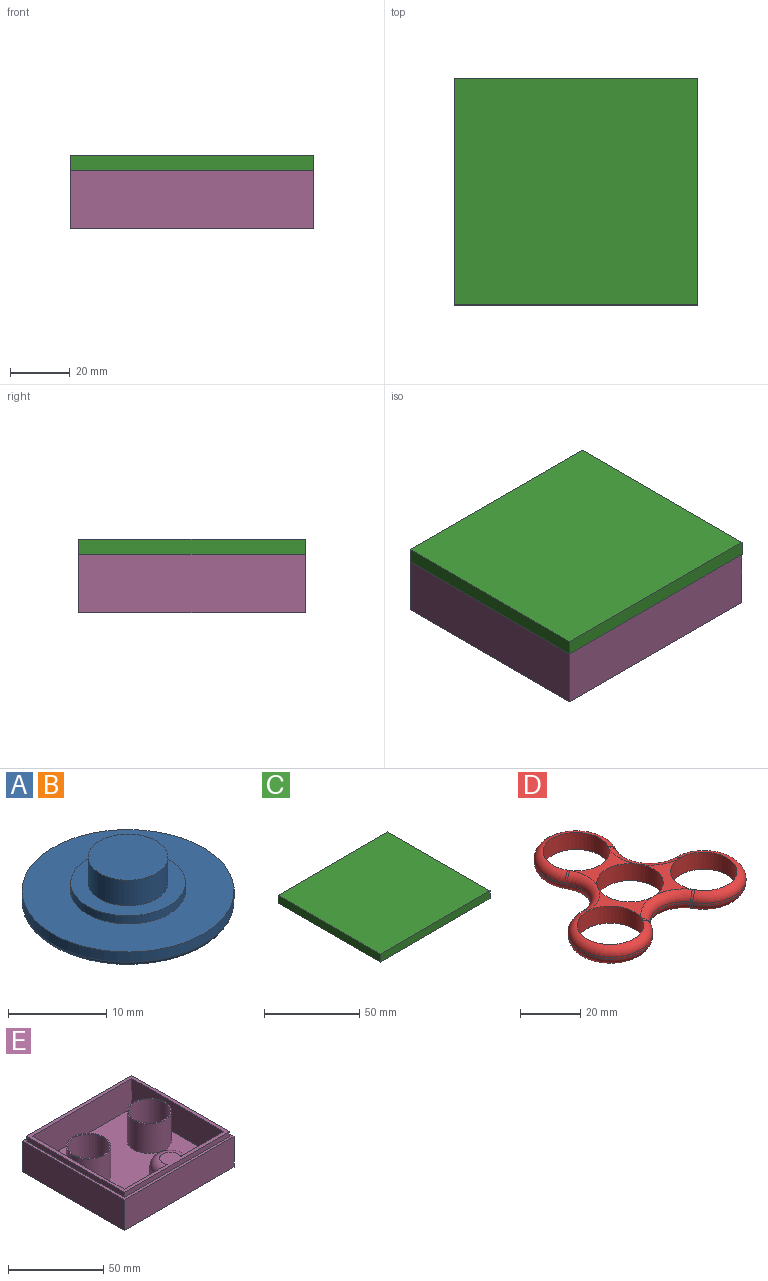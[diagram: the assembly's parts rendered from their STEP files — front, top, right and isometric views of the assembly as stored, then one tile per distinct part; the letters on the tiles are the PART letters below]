
ASSEMBLY  parts=5 mates=4
PART A: 15 faces, bbox 23.4x23.4x6 mm
  f0: plane 20.57x20.57mm, normal (0,0,-1), area 306.2mm2, adj f5,f6,f7,f8,f9,f10,f11
  f1: cylinder r=10.79mm len=21.59mm, axis (0,0,-1), area 86.1mm2, adj f2,f5
  f2: plane 21.59x21.59mm, normal (0,0,1), area 258.9mm2, adj f1,f3
  f3: cylinder r=5.84mm len=11.68mm, axis (0,0,-1), area 37.3mm2, adj f2,f4
  f4: plane 11.68x11.68mm, normal (0,0,1), area 55.2mm2, adj f3,f13
  f5: torus R=10.29mm, axis (0,0,1), area 53.2mm2, adj f0,f1
  f6: plane 9.77x8.45mm, normal (0.65,0.76,0), area 6.6mm2, adj f0,f7,f11,f12
  f7: plane 6.1x0.51mm, normal (0,-1,0), area 3.1mm2, adj f0,f6,f8,f12
  f8: plane 6.49x6.15mm, normal (0.69,0.73,0), area 4.5mm2, adj f0,f7,f9,f12
  f9: plane 10.56x7.83mm, normal (-0.6,-0.8,0), area 6.7mm2, adj f0,f8,f10,f12
  f10: plane 6.1x0.51mm, normal (0,1,0), area 3.1mm2, adj f0,f9,f11,f12
  f11: plane 6.77x5.71mm, normal (-0.76,-0.64,0), area 4.5mm2, adj f0,f6,f10,f12
  f12: plane 14.6x10.56mm, normal (0,0,-1), area 26.2mm2, adj f6,f7,f8,f9,f10,f11
  f13: cylinder r=4.07mm len=8.14mm, axis (0,0,-1), area 81.2mm2, adj f4,f14
  f14: plane 8.14x8.14mm, normal (0,0,1), area 52mm2, adj f13
PART B: same geometry as A
PART C: 6 faces, bbox 81.8x75.9x5.1 mm
  f0: plane 81.79x5.08mm, normal (0,1,0), area 415.5mm2, adj f1,f3,f4,f5
  f1: plane 75.93x5.08mm, normal (-1,0,0), area 385.7mm2, adj f0,f2,f4,f5
  f2: plane 81.79x5.08mm, normal (0,-1,0), area 415.5mm2, adj f1,f3,f4,f5
  f3: plane 75.93x5.08mm, normal (1,0,0), area 385.7mm2, adj f0,f2,f4,f5
  f4: plane 81.79x75.93mm, normal (0,0,1), area 6210.4mm2, adj f0,f1,f2,f3
  f5: plane 81.79x75.93mm, normal (0,0,-1), area 6210.4mm2, adj f0,f1,f2,f3
PART D: 40 faces, bbox 73.9x68.1x7.4 mm
  f0: plane 18.08x12.74mm, normal (0,0,1), area 84.2mm2, adj f9,f12,f30,f38
  f1: plane 22.02x20.07mm, normal (0,0,1), area 84.2mm2, adj f9,f11,f33,f38
  f2: plane 22.02x20.07mm, normal (0,0,-1), area 84.2mm2, adj f9,f10,f23,f24
  f3: plane 22.02x20.07mm, normal (0,0,-1), area 84.2mm2, adj f9,f11,f16,f24
  f4: cylinder r=11.25mm len=16.88mm, axis (0,0,-1), area 19.8mm2, adj f5,f13,f16,f17,f18,f36,f38,f39
  f5: cylinder r=13.97mm len=27.94mm, axis (0,0,-1), area 49.1mm2, adj f4,f6,f20,f37
  f6: cylinder r=11.25mm len=19.49mm, axis (0,0,-1), area 19.8mm2, adj f5,f7,f22,f24,f26,f31,f33,f35
  f7: cylinder r=13.97mm len=27.94mm, axis (0,0,-1), area 49.1mm2, adj f6,f8,f27,f29
  f8: cylinder r=11.26mm len=16.88mm, axis (0,0,-1), area 19.8mm2, adj f7,f13,f21,f23,f25,f28,f30,f32
  f9: cylinder r=10.99mm len=21.97mm, axis (0,0,-1), area 478.6mm2, adj f0,f1,f2,f3,f14,f15,f16,f23
  f10: cylinder r=10.99mm len=21.97mm, axis (0,0,-1), area 478.6mm2, adj f2,f14,f25,f26,f27,f28,f29,f31
  f11: cylinder r=10.99mm len=21.97mm, axis (0,0,-1), area 478.6mm2, adj f1,f3,f18,f20,f22,f35,f37,f39
  f12: cylinder r=10.99mm len=21.97mm, axis (0,0,-1), area 478.6mm2, adj f0,f15,f17,f19,f21,f32,f34,f36
  f13: cylinder r=13.97mm len=27.94mm, axis (0,0,-1), area 49.1mm2, adj f4,f8,f19,f34
  f14: plane 22.02x20.07mm, normal (0,0,1), area 84.2mm2, adj f9,f10,f30,f33
  f15: plane 18.08x12.74mm, normal (0,0,-1), area 84.2mm2, adj f9,f12,f16,f23
  f16: torus R=14.3mm, axis (0,0,1), area 116.6mm2, adj f3,f4,f9,f15,f17,f18
  f17: bspline ~3.88x3.51mm, area 3.6mm2, adj f4,f12,f16,f19
  f18: bspline ~3.16x3.15mm, area 3.6mm2, adj f4,f11,f16,f20
  f19: torus R=10.92mm, axis (0,0,-1), area 255mm2, adj f12,f13,f17,f21
  f20: torus R=10.92mm, axis (0,0,-1), area 255.1mm2, adj f5,f11,f18,f22
  f21: bspline ~3.88x3.51mm, area 3.6mm2, adj f8,f12,f19,f23
  f22: bspline ~3.55x3.38mm, area 3.6mm2, adj f6,f11,f20,f24
  f23: torus R=14.3mm, axis (0,0,1), area 116.6mm2, adj f2,f8,f9,f15,f21,f25
  f24: torus R=14.3mm, axis (0,0,1), area 116.6mm2, adj f2,f3,f6,f9,f22,f26
  f25: bspline ~3.16x3.15mm, area 3.6mm2, adj f8,f10,f23,f27
  f26: bspline ~3.55x3.38mm, area 3.6mm2, adj f6,f10,f24,f27
  f27: torus R=10.92mm, axis (0,0,-1), area 255mm2, adj f7,f10,f25,f26
  f28: bspline ~3.16x3.15mm, area 3.6mm2, adj f8,f10,f29,f30
  f29: torus R=10.92mm, axis (0,0,1), area 255mm2, adj f7,f10,f28,f31
  f30: torus R=14.3mm, axis (0,0,1), area 116.6mm2, adj f0,f8,f9,f14,f28,f32
  f31: bspline ~3.55x3.38mm, area 3.6mm2, adj f6,f10,f29,f33
  f32: bspline ~3.88x3.51mm, area 3.6mm2, adj f8,f12,f30,f34
  f33: torus R=14.3mm, axis (0,0,1), area 116.6mm2, adj f1,f6,f9,f14,f31,f35
  f34: torus R=10.92mm, axis (0,0,1), area 255mm2, adj f12,f13,f32,f36
  f35: bspline ~3.55x3.38mm, area 3.6mm2, adj f6,f11,f33,f37
  f36: bspline ~3.88x3.51mm, area 3.6mm2, adj f4,f12,f34,f38
  f37: torus R=10.92mm, axis (0,0,1), area 255.1mm2, adj f5,f11,f35,f39
  f38: torus R=14.3mm, axis (0,0,1), area 116.6mm2, adj f0,f1,f4,f9,f36,f39
  f39: bspline ~3.16x3.15mm, area 3.6mm2, adj f4,f11,f37,f38
PART E: 27 faces, bbox 81.8x75.9x22.9 mm
  f0: plane 78.23x72.38mm, normal (0,0,1), area 674.6mm2, adj f1,f2,f3,f4,f5,f16,f17,f18
  f1: plane 32.07x19.05mm, normal (0,1,0), area 513.8mm2, adj f0,f5,f6,f15,f16
  f2: plane 32.07x19.05mm, normal (0,1,0), area 513.7mm2, adj f0,f3,f6,f15,f16
  f3: plane 68.31x19.05mm, normal (1,0,0), area 1301.4mm2, adj f0,f2,f4,f6
  f4: plane 74.17x19.05mm, normal (0,-1,0), area 1412.9mm2, adj f0,f3,f5,f6
  f5: plane 68.31x19.05mm, normal (-1,0,0), area 1301.4mm2, adj f0,f1,f4,f6
  f6: plane 74.17x68.31mm, normal (0,0,1), area 3971.7mm2, adj f1,f2,f3,f4,f5,f8,f12,f15
  f7: cylinder r=11.05mm len=22.1mm, axis (0,0,-1), area 1322.5mm2, adj f9,f10
  f8: cylinder r=11.68mm len=23.37mm, axis (0,0,-1), area 1398.5mm2, adj f6,f9
  f9: plane 23.37x23.37mm, normal (0,0,1), area 45.4mm2, adj f7,f8
  f10: plane 22.1x22.1mm, normal (0,0,1), area 383.5mm2, adj f7
  f11: cylinder r=11.05mm len=22.1mm, axis (0,0,-1), area 1322.5mm2, adj f13,f14
  f12: cylinder r=11.68mm len=23.37mm, axis (0,0,-1), area 1398.5mm2, adj f6,f13
  f13: plane 23.37x23.37mm, normal (0,0,1), area 45.4mm2, adj f11,f12
  f14: plane 22.1x22.1mm, normal (0,0,1), area 383.5mm2, adj f11
  f15: cylinder r=10.74mm len=21.49mm, axis (0,0,-1), area 545.7mm2, adj f1,f2,f6,f16
  f16: torus R=5.66mm, axis (0,0,1), area 265.7mm2, adj f0,f1,f2,f15
  f17: plane 72.38x3.18mm, normal (-1,0,0), area 229.8mm2, adj f0,f18,f20,f21
  f18: plane 78.23x3.18mm, normal (0,1,0), area 248.4mm2, adj f0,f17,f19,f21
  f19: plane 72.38x3.18mm, normal (1,0,0), area 229.8mm2, adj f0,f18,f20,f21
  f20: plane 78.23x3.18mm, normal (0,-1,0), area 248.4mm2, adj f0,f17,f19,f21
  f21: plane 81.79x75.93mm, normal (0,0,1), area 548.2mm2, adj f17,f18,f19,f20,f23,f24,f25,f26
  f22: plane 81.79x75.93mm, normal (0,0,-1), area 6210.4mm2, adj f23,f24,f25,f26
  f23: plane 81.79x19.69mm, normal (0,1,0), area 1610mm2, adj f21,f22,f24,f26
  f24: plane 75.93x19.69mm, normal (1,0,0), area 1494.7mm2, adj f21,f22,f23,f25
  f25: plane 81.79x19.69mm, normal (0,-1,0), area 1610mm2, adj f21,f22,f24,f26
  f26: plane 75.93x19.69mm, normal (-1,0,0), area 1494.7mm2, adj f21,f22,f23,f25
PLACE A t=(-24.63,14.39,0.91)mm
PLACE B t=(20.66,14.46,0)mm
PLACE C t=(-0.39,12.16,11.3)mm
PLACE D t=(-2.78,1.78,4.24)mm
PLACE E t=(-1.96,-0.65,-4.57)mm
MATE cylindrical E.f7 <-> B.f1  axis (0,0,-1) through (20.66,14.46,4.95)mm
MATE cylindrical D.f4 <-> E.f11  axis (0,0,1) through (-24.63,14.39,8.13)mm
MATE cylindrical A.f1 <-> E.f11  axis (0,0,-1) through (-24.63,14.39,2.06)mm
MATE fastened C.f5 <-> E.f21  axis (0,0,1) through (-42.86,-30.33,11.3)mm
